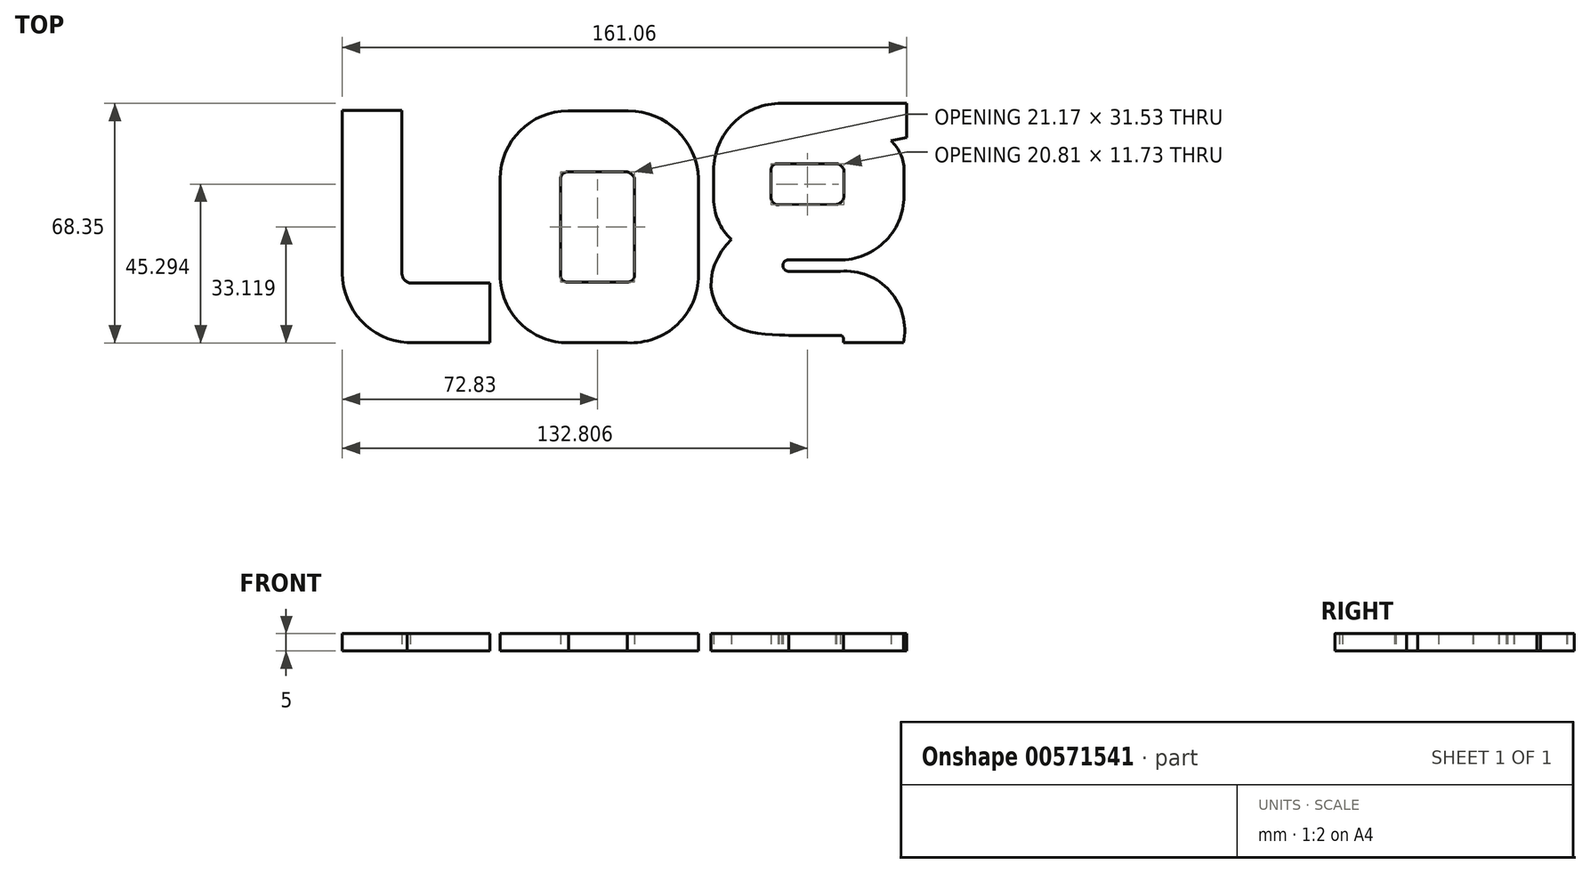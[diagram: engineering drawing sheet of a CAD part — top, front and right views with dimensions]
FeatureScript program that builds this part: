
annotation { "Feature Type Name" : "Feature", "Feature Type Description" : "" }
export const myFeature = defineFeature(function(context is Context, id is Id, definition is map)
    precondition{}
    {
        {
            var Q0;
            Q0=qCreatedBy(makeId("Top.planeOp"),FACE);
            var sketch = newSketch(context, id + "F0", { "sketchPlane" : qUnion([Q0])});
            skLineSegment(sketch, "E0", {"start": v(-72.78, 34.43) * mm, "end": v(-55.78, 34.43) * mm});
            skLineSegment(sketch, "E1", {"start": v(-55.78, 34.43) * mm, "end": v(-55.78, -11.93) * mm});
            skLineSegment(sketch, "E2", {"start": v(-53.42, -14.84) * mm, "end": v(-30.72, -14.84) * mm});
            skLineSegment(sketch, "E3", {"start": v(-30.72, -14.84) * mm, "end": v(-30.72, -31.84) * mm});
            skLineSegment(sketch, "E4", {"start": v(-30.72, -31.84) * mm, "end": v(-54.26, -31.84) * mm});
            skLineSegment(sketch, "E5", {"start": v(-72.78, -11.93) * mm, "end": v(-72.78, 34.43) * mm});
            skLineSegment(sketch, "E6.bottom", {"start": v(-8.31, 17.01) * mm, "end": v(7.86, 17.01) * mm});
            skLineSegment(sketch, "E6.top", {"start": v(-8.31, 34.37) * mm, "end": v(8.86, 34.37) * mm});
            skLineSegment(sketch, "E7.left", {"start": v(-10.53, 14.93) * mm, "end": v(-10.53, -12.55) * mm});
            skLineSegment(sketch, "E7.right", {"start": v(-27.75, 14.93) * mm, "end": v(-27.75, -12.55) * mm});
            skLineSegment(sketch, "E8.left", {"start": v(10.63, 15) * mm, "end": v(10.63, -12.55) * mm});
            skLineSegment(sketch, "E8.right", {"start": v(28.92, 15) * mm, "end": v(28.92, -12.55) * mm});
            skLineSegment(sketch, "E9.bottom", {"start": v(-8.24, -14.5) * mm, "end": v(8.55, -14.5) * mm});
            skLineSegment(sketch, "E9.top", {"start": v(-8.24, -31.84) * mm, "end": v(8.55, -31.84) * mm});
            skLineSegment(sketch, "E10.bottom", {"start": v(52.6, 36.48) * mm, "end": v(69.03, 36.48) * mm});
            skLineSegment(sketch, "E10.top", {"start": v(51.6, 19.27) * mm, "end": v(68.03, 19.27) * mm});
            skLineSegment(sketch, "E11.bottom", {"start": v(51.84, 7.56) * mm, "end": v(68.27, 7.64) * mm});
            skLineSegment(sketch, "E12.left", {"start": v(49.62, 17.35) * mm, "end": v(49.62, 9.59) * mm});
            skLineSegment(sketch, "E12.right", {"start": v(33.23, 17.35) * mm, "end": v(33.23, 9.24) * mm});
            skLineSegment(sketch, "E13.left", {"start": v(70.43, 17.41) * mm, "end": v(70.43, 10.1) * mm});
            skLineSegment(sketch, "E13.right", {"start": v(87.57, 17.41) * mm, "end": v(87.57, 10.1) * mm});
            skLineSegment(sketch, "E14", {"start": v(54.64, -8.16) * mm, "end": v(68.03, -8.17) * mm});
            skLineSegment(sketch, "E15", {"start": v(54.64, -11.44) * mm, "end": v(69.37, -11.44) * mm});
            skLineSegment(sketch, "E16", {"start": v(69.37, -29.72) * mm, "end": v(54.64, -29.72) * mm});
            skLineSegment(sketch, "E17", {"start": v(70.23, -31.84) * mm, "end": v(87.41, -31.84) * mm});
            skLineSegment(sketch, "E18", {"start": v(38.18, -2.31) * mm, "end": v(38.27, -2.31) * mm});
            skLineSegment(sketch, "E19", {"start": v(69.03, 36.48) * mm, "end": v(88.28, 36.48) * mm});
            skLineSegment(sketch, "E20", {"start": v(88.28, 36.48) * mm, "end": v(88.28, 26.79) * mm});
            skLineSegment(sketch, "E21", {"start": v(88.28, 26.79) * mm, "end": v(83.83, 25.84) * mm});
            skArc(sketch, "E22", {"start": v(52.6, 36.48) * mm, "mid": v(38.91, 30.96) * mm, "end": v(33.23, 17.35) * mm});
            skArc(sketch, "E23", {"start": v(33.23, 9.24) * mm, "mid": v(34.54, 2.94) * mm, "end": v(38.27, -2.31) * mm});
            skArc(sketch, "E24", {"start": v(87.57, 17.41) * mm, "mid": v(86.6, 22.02) * mm, "end": v(83.83, 25.84) * mm});
            skArc(sketch, "E25", {"start": v(68.03, -8.17) * mm, "mid": v(81.76, -3.28) * mm, "end": v(87.57, 10.1) * mm});
            skFitSpline(sketch, "E26", {"points": [v(38.27, -2.31) * mm, v(32.47, -14.8) * mm, v(36.7, -25.04) * mm, v(44.74, -28.92) * mm, v(54.64, -29.72) * mm], "startDerivative": vector(-34.34, -31.99) * mm, "endDerivative": vector(17.88, -0.3) * mm});
            skArc(sketch, "E27", {"start": v(87.41, -31.84) * mm, "mid": v(83.55, -17.08) * mm, "end": v(69.37, -11.44) * mm});
            skArc(sketch, "E28", {"start": v(54.64, -8.16) * mm, "mid": v(53, -9.8) * mm, "end": v(54.64, -11.44) * mm});
            skArc(sketch, "E29", {"start": v(70.43, 10.1) * mm, "mid": v(69.82, 8.46) * mm, "end": v(68.27, 7.64) * mm});
            skArc(sketch, "E30", {"start": v(68.03, 19.27) * mm, "mid": v(69.54, 18.75) * mm, "end": v(70.43, 17.41) * mm});
            skArc(sketch, "E31", {"start": v(51.64, 19.27) * mm, "mid": v(50.15, 18.81) * mm, "end": v(49.62, 17.35) * mm});
            skLineSegment(sketch, "E32", {"start": v(70.23, -31.84) * mm, "end": v(70.24, -30.55) * mm});
            skArc(sketch, "E33", {"start": v(-55.78, -11.93) * mm, "mid": v(-55.12, -13.8) * mm, "end": v(-53.42, -14.84) * mm});
            skArc(sketch, "E34", {"start": v(-72.78, -11.93) * mm, "mid": v(-67.43, -25.53) * mm, "end": v(-54.26, -31.84) * mm});
            skArc(sketch, "E35", {"start": v(-10.53, -12.55) * mm, "mid": v(-9.84, -14.05) * mm, "end": v(-8.24, -14.5) * mm});
            skArc(sketch, "E36", {"start": v(-27.75, -12.55) * mm, "mid": v(-22.02, -26.27) * mm, "end": v(-8.24, -31.84) * mm});
            skArc(sketch, "E37", {"start": v(10.63, -12.55) * mm, "mid": v(10.02, -13.97) * mm, "end": v(8.55, -14.5) * mm});
            skArc(sketch, "E38", {"start": v(28.92, -12.55) * mm, "mid": v(22.88, -26.58) * mm, "end": v(8.55, -31.84) * mm});
            skArc(sketch, "E39", {"start": v(8.86, 34.37) * mm, "mid": v(22.8, 28.73) * mm, "end": v(28.92, 15) * mm});
            skArc(sketch, "E40", {"start": v(7.86, 17.01) * mm, "mid": v(9.57, 16.46) * mm, "end": v(10.63, 15) * mm});
            skArc(sketch, "E41", {"start": v(-8.31, 17.01) * mm, "mid": v(-9.83, 16.41) * mm, "end": v(-10.53, 14.93) * mm});
            skArc(sketch, "E42", {"start": v(-8.31, 34.37) * mm, "mid": v(-22.05, 28.67) * mm, "end": v(-27.75, 14.93) * mm});
            skArc(sketch, "E43", {"start": v(49.62, 9.59) * mm, "mid": v(50.28, 8.08) * mm, "end": v(51.84, 7.56) * mm});
            skArc(sketch, "E44", {"start": v(69.37, -29.72) * mm, "mid": v(69.97, -29.96) * mm, "end": v(70.24, -30.55) * mm});
            skLineSegment(sketch, "E45", {"start": v(-64.28, 35.56) * mm, "end": v(-64.28, -37.4) * mm, "construction": true});
            skPoint(sketch, "E45.startSnap0", {"position": v(-64.28, 34.43) * mm});
            skLineSegment(sketch, "E46", {"start": v(-30.72, -23.34) * mm, "end": v(-73.09, -23.34) * mm, "construction": true});
            skLineSegment(sketch, "E47.MirrorCS", {"start": v(-72.78, 34.43) * mm, "end": v(-72.78, -11.93) * mm});
            skLineSegment(sketch, "E48.MirrorCS", {"start": v(-55.78, -11.93) * mm, "end": v(-55.78, 34.43) * mm});
            skSolve(sketch);
        }
        {
            var Q0;
            Q0=makeQuery(id+"F0.imprint","IMPRINT",FACE,{"disambiguationData":[TD([[makeQuery(id+"F0.imprint","IMPRINT",EDGE,{"derivedFrom":sQuery(id+"F0.wireOp",EDGE,"E10.bottom")}),-1.0]])]});
            var Q1;
            Q1=makeQuery(id+"F0.imprint","IMPRINT",FACE,{"disambiguationData":[TD([[makeQuery(id+"F0.imprint","IMPRINT",EDGE,{"derivedFrom":sQuery(id+"F0.wireOp",EDGE,"E6.bottom")}),1.0]])]});
            var Q2;
            Q2=makeQuery(id+"F0.imprint","IMPRINT",FACE,{"disambiguationData":[TD([[makeQuery(id+"F0.imprint","IMPRINT",EDGE,{"derivedFrom":sQuery(id+"F0.wireOp",EDGE,"E0")}),-1.0]])]});
            extrude(context, id + "F1", {"entities" : qUnion([Q0, Q1, Q2]), "depth" : 5 * mm, "offsetDistance" : 25 * mm});
        }
    });
